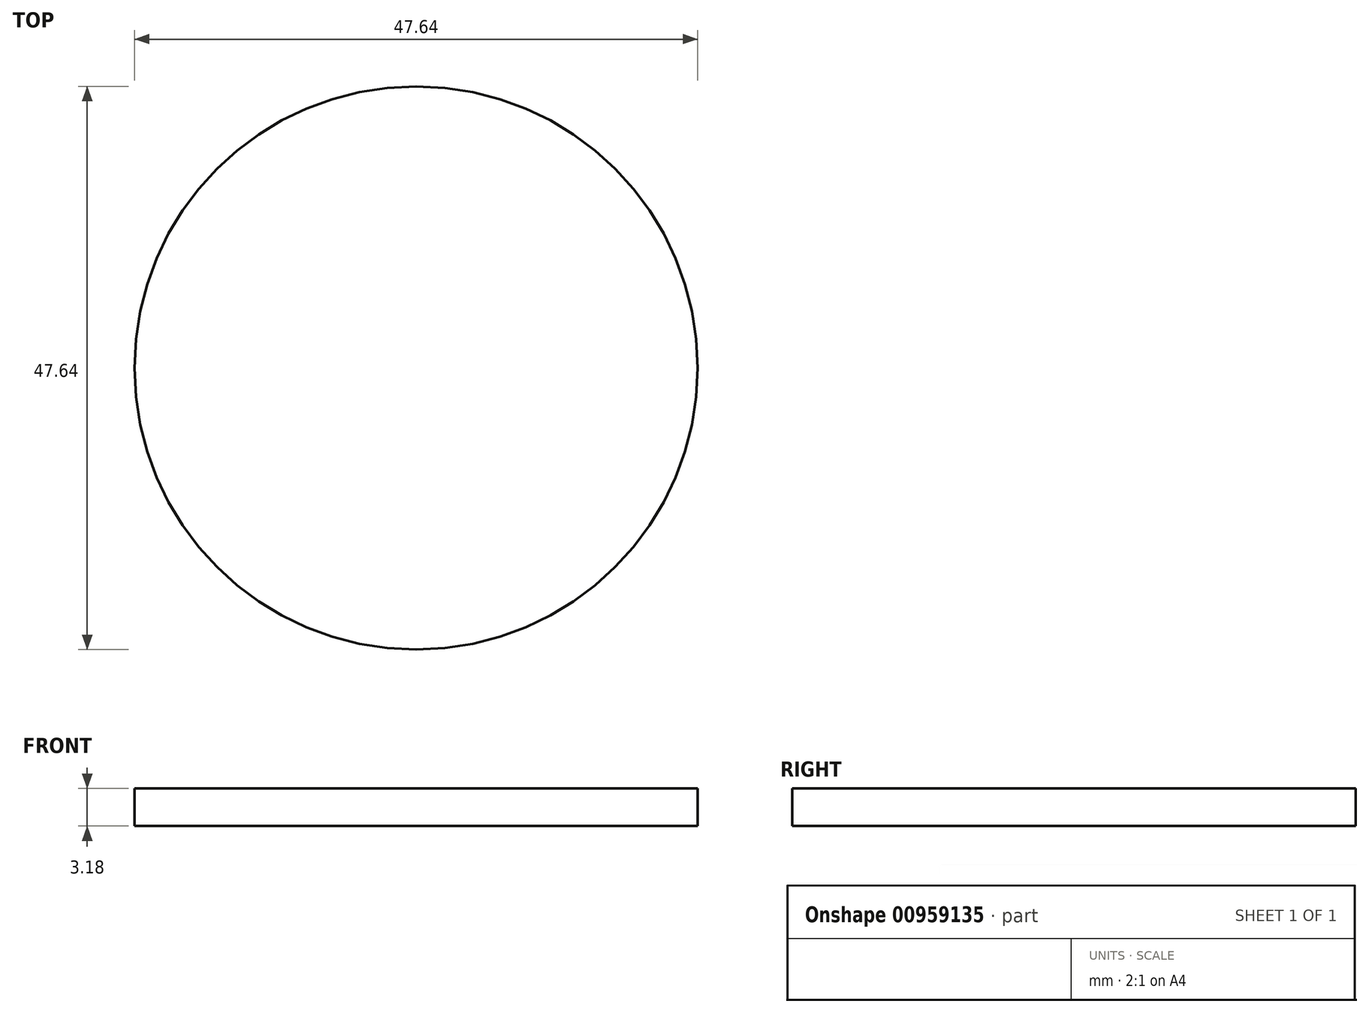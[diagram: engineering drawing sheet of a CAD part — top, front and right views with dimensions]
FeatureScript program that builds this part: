
annotation { "Feature Type Name" : "Feature", "Feature Type Description" : "" }
export const myFeature = defineFeature(function(context is Context, id is Id, definition is map)
    precondition{}
    {
        {
            var Q0;
            Q0=qCreatedBy(makeId("Top.planeOp"),FACE);
            var sketch = newSketch(context, id + "F0", { "sketchPlane" : qUnion([Q0])});
            skCircle(sketch, "E0", {"center": v(0, 0) * mm, "radius": 23.82 * mm});
            skSolve(sketch);
        }
        {
            var Q0;
            Q0=qSketchRegion(id+"F0",true);
            extrude(context, id + "F1", {"entities" : qUnion([Q0]), "depth" : 3.17 * mm, "offsetDistance" : 25.4 * mm});
        }
    });
